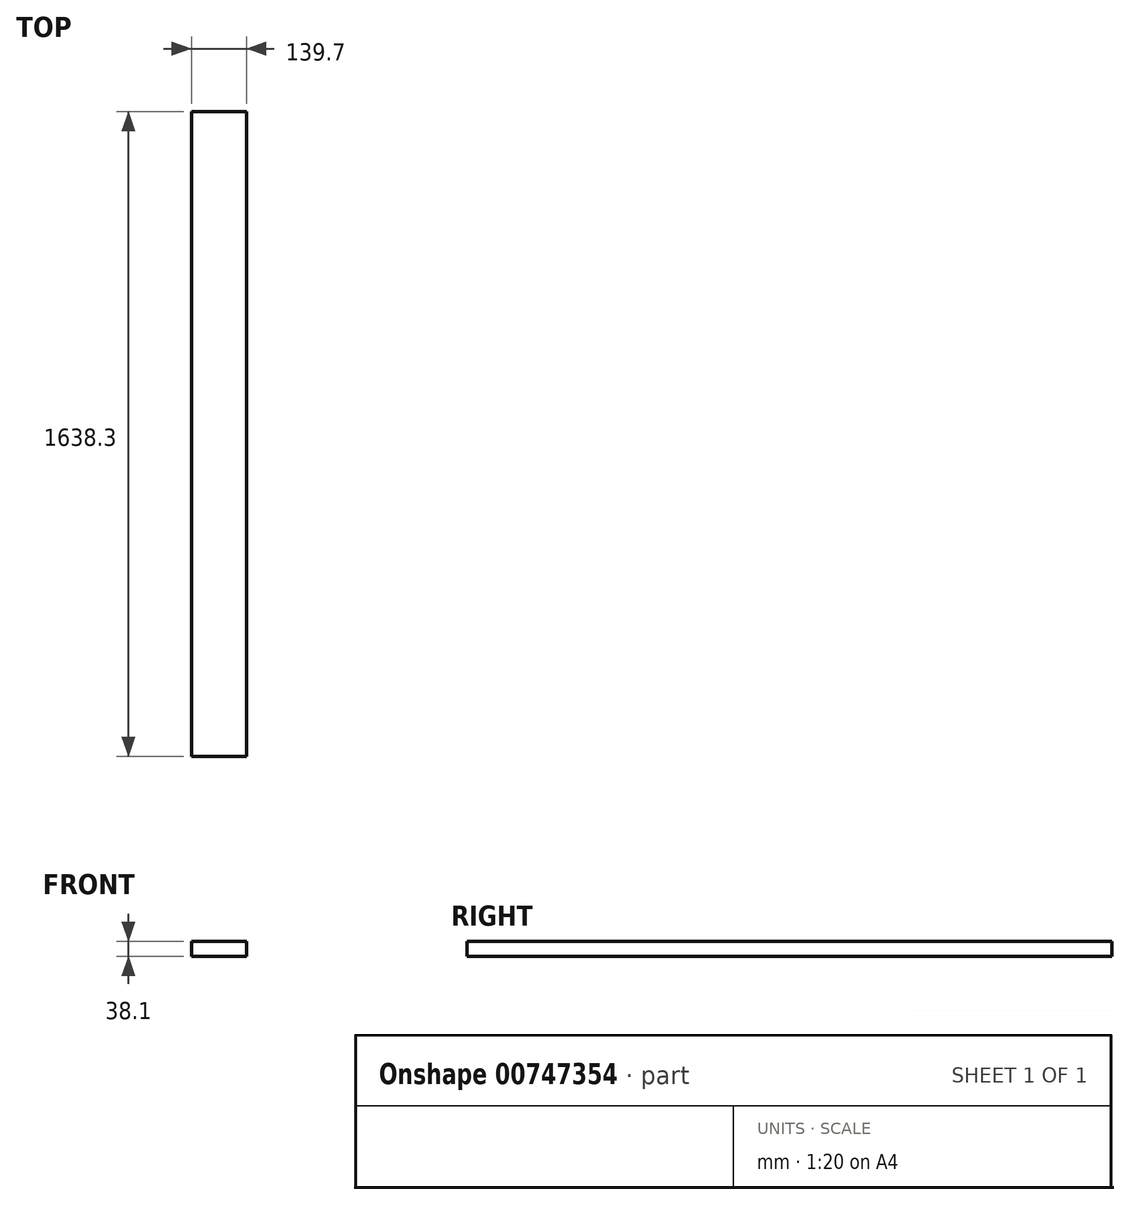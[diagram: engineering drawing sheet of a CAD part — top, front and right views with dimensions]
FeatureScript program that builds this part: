
annotation { "Feature Type Name" : "Feature", "Feature Type Description" : "" }
export const myFeature = defineFeature(function(context is Context, id is Id, definition is map)
    precondition{}
    {
        {
            var Q0;
            Q0=qCreatedBy(makeId("Front.planeOp"),FACE);
            var sketch = newSketch(context, id + "F0", { "sketchPlane" : qUnion([Q0])});
            skLineSegment(sketch, "E0.bottom", {"start": v(0, 0) * mm, "end": v(139.7, 0) * mm});
            skLineSegment(sketch, "E0.top", {"start": v(0, 38.1) * mm, "end": v(139.7, 38.1) * mm});
            skLineSegment(sketch, "E0.left", {"start": v(0, 0) * mm, "end": v(0, 38.1) * mm});
            skLineSegment(sketch, "E0.right", {"start": v(139.7, 0) * mm, "end": v(139.7, 38.1) * mm});
            skSolve(sketch);
        }
        {
            var Q0;
            Q0=qSketchRegion(id+"F0",true);
            extrude(context, id + "F1", {"entities" : qUnion([Q0]), "depth" : 1638.3 * mm, "offsetDistance" : 25.4 * mm});
        }
    });
